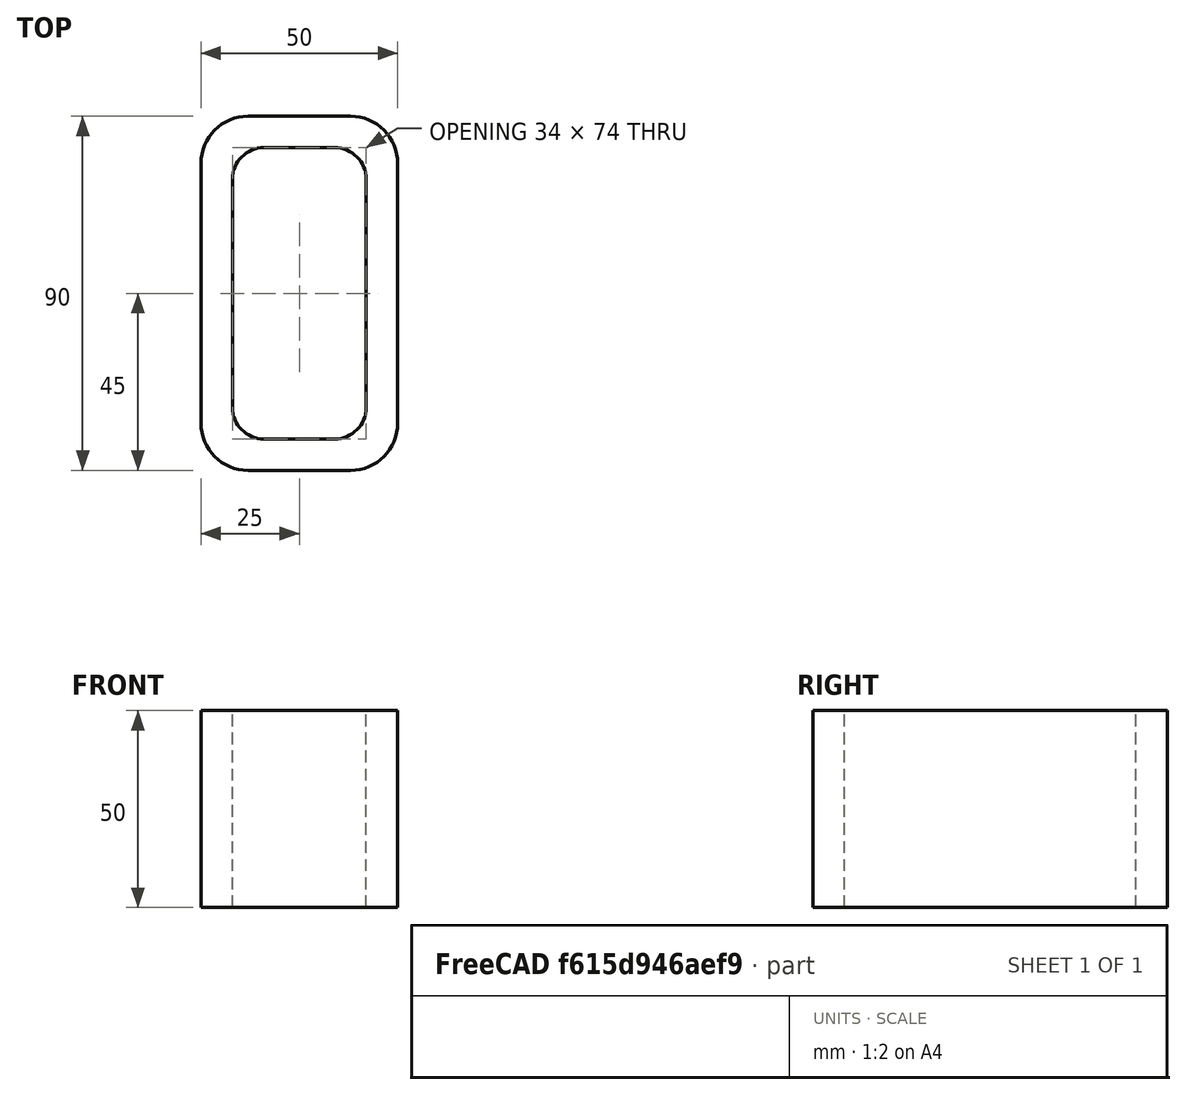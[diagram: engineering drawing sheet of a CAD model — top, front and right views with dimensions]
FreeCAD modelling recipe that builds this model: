
FCSTD DOCUMENT  (FreeCAD 0.15R4671 (Git))
Label: Rectangular hollow section 90x50x8 EN10219 S235JRH
License: All rights reserved
LicenseURL: http://en.wikipedia.org/wiki/All_rights_reserved
objects: Sketcher::SketchObject×1, Part::Extrusion×1
note: 2 computed .brp shape members not serialized (recipe doc carries the construction recipe); baked Part::Feature solids carry a one-line shape summary decoded from their .brp

FEATURE [Sketcher::SketchObject] Sketch
  sketch-geometry (16):
    g0: LineSegment StartX=-9 StartY=37 StartZ=0 EndX=9 EndY=37 EndZ=0
    g1: LineSegment StartX=17 StartY=29 StartZ=0 EndX=17 EndY=-29 EndZ=0
    g2: LineSegment StartX=9 StartY=-37 StartZ=0 EndX=-9 EndY=-37 EndZ=0
    g3: LineSegment StartX=-17 StartY=-29 StartZ=0 EndX=-17 EndY=29 EndZ=0
    g4: LineSegment StartX=-13 StartY=45 StartZ=0 EndX=13 EndY=45 EndZ=0
    g5: LineSegment StartX=25 StartY=33 StartZ=0 EndX=25 EndY=-33 EndZ=0
    g6: LineSegment StartX=13 StartY=-45 StartZ=0 EndX=-13 EndY=-45 EndZ=0
    g7: LineSegment StartX=-25 StartY=-33 StartZ=0 EndX=-25 EndY=33 EndZ=0
    g8: ArcOfCircle CenterX=-9 CenterY=29 CenterZ=0 NormalX=0 NormalY=0 NormalZ=1 Radius=8 StartAngle=1.5708 EndAngle=3.14159
    g9: ArcOfCircle CenterX=9 CenterY=29 CenterZ=0 NormalX=0 NormalY=0 NormalZ=1 Radius=8 StartAngle=0 EndAngle=1.5708
    g10: ArcOfCircle CenterX=9 CenterY=-29 CenterZ=0 NormalX=0 NormalY=0 NormalZ=1 Radius=8 StartAngle=4.71239 EndAngle=6.28319
    g11: ArcOfCircle CenterX=-9 CenterY=-29 CenterZ=0 NormalX=0 NormalY=0 NormalZ=1 Radius=8 StartAngle=3.14159 EndAngle=4.71239
    g12: ArcOfCircle CenterX=13 CenterY=33 CenterZ=0 NormalX=0 NormalY=0 NormalZ=1 Radius=12 StartAngle=0 EndAngle=1.5708
    g13: ArcOfCircle CenterX=13 CenterY=-33 CenterZ=0 NormalX=0 NormalY=0 NormalZ=1 Radius=12 StartAngle=4.71239 EndAngle=6.28319
    g14: ArcOfCircle CenterX=-13 CenterY=-33 CenterZ=0 NormalX=0 NormalY=0 NormalZ=1 Radius=12 StartAngle=3.14159 EndAngle=4.71239
    g15: ArcOfCircle CenterX=-13 CenterY=33 CenterZ=0 NormalX=0 NormalY=0 NormalZ=1 Radius=12 StartAngle=1.5708 EndAngle=3.14159
  constraints (36):
    c: Horizontal(g2)
    c: Vertical(g3)
    c: Horizontal(g6)
    c: Vertical(g7)
    c: Tangent(g3,g8) = 1.5708
    c: Tangent(g0,g8) = 1.5708
    c: Tangent(g0,g9) = 1.5708
    c: Tangent(g1,g9) = 1.5708
    c: Tangent(g1,g10) = 1.5708
    c: Tangent(g2,g10) = 1.5708
    c: Tangent(g2,g11) = 1.5708
    c: Tangent(g3,g11) = 1.5708
    c: Tangent(g4,g12) = 1.5708
    c: Tangent(g5,g12) = 1.5708
    c: Tangent(g5,g13) = 1.5708
    c: Tangent(g6,g13) = 1.5708
    c: Tangent(g6,g14) = 1.5708
    c: Tangent(g7,g14) = 1.5708
    c: Tangent(g7,g15) = 1.5708
    c: Tangent(g4,g15) = 1.5708
    c: Equal(g9,g8)
    c: Equal(g9,g11)
    c: Equal(g9,g10)
    c: Equal(g12,g15)
    c: Equal(g12,g14)
    c: Equal(g12,g13)
    c: Symmetric(g4,g6,g-1)
    c: Symmetric(g7,g5,g-2)
    c: DistanceY(g4,g6) = -90
    c: DistanceX(g7,g5) = 50
    c: Symmetric(g3,g1,g-2)
    c: Symmetric(g0,g2,g-1)
    c: DistanceY(g0,g4) = 8
    c: DistanceX(g5,g1) = -8
    c: Radius(g9) = 8
    c: Radius(g12) = 12
FEATURE [Part::Extrusion] Extrude  label="Rectangular hollow section 90x50x8 EN10219 S235JRH"
  Base = -> Sketch
  Dir = (0,0,50)
  Solid = true
